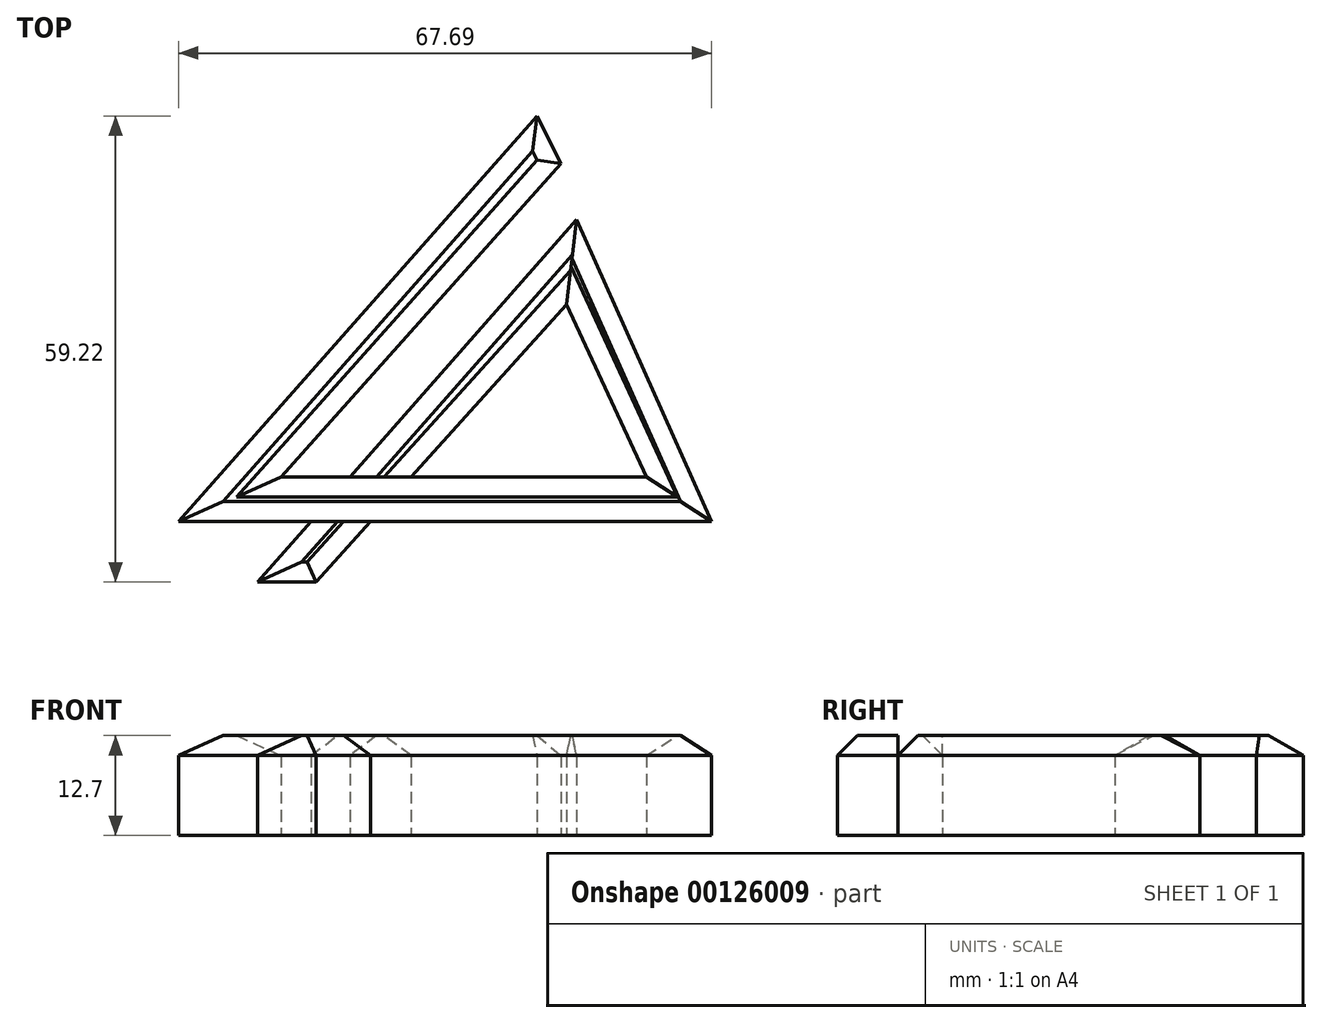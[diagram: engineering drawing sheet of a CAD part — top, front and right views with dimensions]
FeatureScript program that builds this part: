
annotation { "Feature Type Name" : "Feature", "Feature Type Description" : "" }
export const myFeature = defineFeature(function(context is Context, id is Id, definition is map)
    precondition{}
    {
        {
            var Q0;
            Q0=qCreatedBy(makeId("Top.planeOp"),FACE);
            var sketch = newSketch(context, id + "F0", { "sketchPlane" : qUnion([Q0])});
            skLineSegment(sketch, "E0", {"start": v(-19.1, 45.5) * mm, "end": v(-54.66, 5.67) * mm});
            skLineSegment(sketch, "E1", {"start": v(-59.72, 0) * mm, "end": v(0, 0) * mm});
            skLineSegment(sketch, "E2", {"start": v(0, 0) * mm, "end": v(-17.14, 38.35) * mm});
            skLineSegment(sketch, "E3", {"start": v(-17.14, 38.35) * mm, "end": v(-57.65, -7.69) * mm});
            skLineSegment(sketch, "E4", {"start": v(-57.65, -7.69) * mm, "end": v(-50.23, -7.69) * mm});
            skLineSegment(sketch, "E5", {"start": v(-50.23, -7.69) * mm, "end": v(-18.4, 27.56) * mm});
            skLineSegment(sketch, "E6", {"start": v(-18.4, 27.56) * mm, "end": v(-8.28, 5.67) * mm});
            skLineSegment(sketch, "E7", {"start": v(-8.28, 5.67) * mm, "end": v(-54.66, 5.67) * mm});
            skLineSegment(sketch, "E8", {"start": v(-19.1, 45.5) * mm, "end": v(-22.13, 51.53) * mm});
            skLineSegment(sketch, "E9", {"start": v(-22.13, 51.53) * mm, "end": v(-67.69, 0) * mm});
            skLineSegment(sketch, "E10", {"start": v(-67.69, 0) * mm, "end": v(-59.72, 0) * mm});
            skLineSegment(sketch, "E11", {"start": v(-17.14, 38.35) * mm, "end": v(-18.4, 27.56) * mm});
            skSolve(sketch);
        }
        {
            var Q0;
            {var subQ0=sQuery(id+"F0.wireOp",EDGE,"E11");Q0=makeQuery(id+"F0.imprint","IMPRINT",FACE,{"disambiguationData":[TD([[makeQuery(id+"F0.imprint","IMPRINT",EDGE,{"derivedFrom":subQ0}),-1.0]])]});}
            var Q1;
            {var subQ5=sQuery(id+"F0.wireOp",EDGE,"E4");Q1=makeQuery(id+"F0.imprint","IMPRINT",FACE,{"disambiguationData":[TD([[makeQuery(id+"F0.imprint","IMPRINT",EDGE,{"derivedFrom":subQ5}),1.0]])]});}
            extrude(context, id + "F1", {"entities" : qUnion([Q0, Q1]), "depth" : 12.7 * mm});
        }
        {
            var Q0;
            {var subQ6=sQuery(id+"F0.wireOp",EDGE,"E2");Q0=makeQuery(id+"F0.imprint","IMPRINT",FACE,{"disambiguationData":[TD([[makeQuery(id+"F0.imprint","IMPRINT",EDGE,{"derivedFrom":subQ6}),1.0]])]});}
            var Q1;
            {var subQ0=sQuery(id+"F0.wireOp",EDGE,"E3");var subQ1=sQuery(id+"F0.wireOp",EDGE,"E1");var subQ2=makeQuery(id+"F0.imprint","INTERSECT",VERTEX,{"derivedFrom":[subQ1,subQ0]});Q1=makeQuery(id+"F0.imprint","IMPRINT",FACE,{"disambiguationData":[TD([[makeQuery(id+"F0.imprint","IMPRINT",EDGE,{"disambiguationData":[TD([[subQ2,-1.0]])],"derivedFrom":subQ1}),1.0]])]});}
            var Q2;
            {var subQ1=sQuery(id+"F0.wireOp",EDGE,"E0");Q2=makeQuery(id+"F0.imprint","IMPRINT",FACE,{"disambiguationData":[TD([[makeQuery(id+"F0.imprint","IMPRINT",EDGE,{"derivedFrom":subQ1}),-1.0]])]});}
            extrude(context, id + "F2", {"entities" : qUnion([Q0, Q1, Q2]), "depth" : 12.7 * mm});
        }
        {
            var Q0;
            Q0=makeQuery(id+"F2.opExtrude","CAP_EDGE",EDGE,{"disambiguationData":[OSD([sQuery(id+"F0.wireOp",EDGE,"E1"),sQuery(id+"F0.wireOp",EDGE,"E10")])],"isStart":false});
            var Q1;
            Q1=makeQuery(id+"F2.opExtrude","CAP_EDGE",EDGE,{"disambiguationData":[OSD([sQuery(id+"F0.wireOp",EDGE,"E7")])],"isStart":false});
            var Q2;
            Q2=makeQuery(id+"F2.opExtrude","CAP_EDGE",EDGE,{"disambiguationData":[OSD([sQuery(id+"F0.wireOp",EDGE,"E6")])],"isStart":false});
            var Q3;
            Q3=makeQuery(id+"F2.opExtrude","CAP_EDGE",EDGE,{"disambiguationData":[OSD([sQuery(id+"F0.wireOp",EDGE,"E2")])],"isStart":false});
            var Q4;
            Q4=makeQuery(id+"F2.opExtrude","CAP_EDGE",EDGE,{"disambiguationData":[OSD([sQuery(id+"F0.wireOp",EDGE,"E9")])],"isStart":false});
            var Q5;
            Q5=makeQuery(id+"F2.opExtrude","CAP_EDGE",EDGE,{"disambiguationData":[OSD([sQuery(id+"F0.wireOp",EDGE,"E0")])],"isStart":false});
            var Q6;
            Q6=makeQuery(id+"F2.opExtrude","CAP_EDGE",EDGE,{"disambiguationData":[OSD([sQuery(id+"F0.wireOp",EDGE,"E8")])],"isStart":false});
            var Q7;
            {var subQ0=sQuery(id+"F0.wireOp",EDGE,"E5");Q7=makeQuery(id+"F1.opExtrude","CAP_EDGE",EDGE,{"disambiguationData":[OSD([subQ0]),TDD([makeQuery(id+"F0.imprint","IMPRINT",EDGE,{"disambiguationData":[TD([[makeQuery(id+"F0.imprint","INTERSECT",VERTEX,{"derivedFrom":[subQ0,sQuery(id+"F0.wireOp",EDGE,"E7")]}),-1.0]])],"derivedFrom":subQ0})])],"isStart":false});}
            var Q8;
            {var subQ0=sQuery(id+"F0.wireOp",EDGE,"E3");Q8=makeQuery(id+"F1.opExtrude","CAP_EDGE",EDGE,{"disambiguationData":[OSD([subQ0]),TDD([makeQuery(id+"F0.imprint","IMPRINT",EDGE,{"disambiguationData":[TD([[makeQuery(id+"F0.imprint","INTERSECT",VERTEX,{"derivedFrom":[subQ0,sQuery(id+"F0.wireOp",EDGE,"E7")]}),1.0]])],"derivedFrom":subQ0})])],"isStart":false});}
            var Q9;
            {var subQ0=sQuery(id+"F0.wireOp",EDGE,"E5");Q9=makeQuery(id+"F1.opExtrude","CAP_EDGE",EDGE,{"disambiguationData":[OSD([subQ0]),TDD([makeQuery(id+"F0.imprint","IMPRINT",EDGE,{"disambiguationData":[TD([[makeQuery(id+"F0.imprint","INTERSECT",VERTEX,{"derivedFrom":[sQuery(id+"F0.wireOp",EDGE,"E4"),subQ0]}),-1.0]])],"derivedFrom":subQ0})])],"isStart":false});}
            var Q10;
            {var subQ0=sQuery(id+"F0.wireOp",EDGE,"E3");Q10=makeQuery(id+"F1.opExtrude","CAP_EDGE",EDGE,{"disambiguationData":[OSD([subQ0]),TDD([makeQuery(id+"F0.imprint","IMPRINT",EDGE,{"disambiguationData":[TD([[makeQuery(id+"F0.imprint","INTERSECT",VERTEX,{"derivedFrom":[subQ0,sQuery(id+"F0.wireOp",EDGE,"E4")]}),1.0]])],"derivedFrom":subQ0})])],"isStart":false});}
            var Q11;
            Q11=makeQuery(id+"F1.opExtrude","CAP_EDGE",EDGE,{"disambiguationData":[OSD([sQuery(id+"F0.wireOp",EDGE,"E4")])],"isStart":false});
            chamfer(context, id + "F3", {"entities" : qUnion([Q0, Q1, Q2, Q3, Q4, Q5, Q6, Q7, Q8, Q9, Q10, Q11]), "width" : 2.54 * mm, "tangentPropagation" : true});
        }
    });
